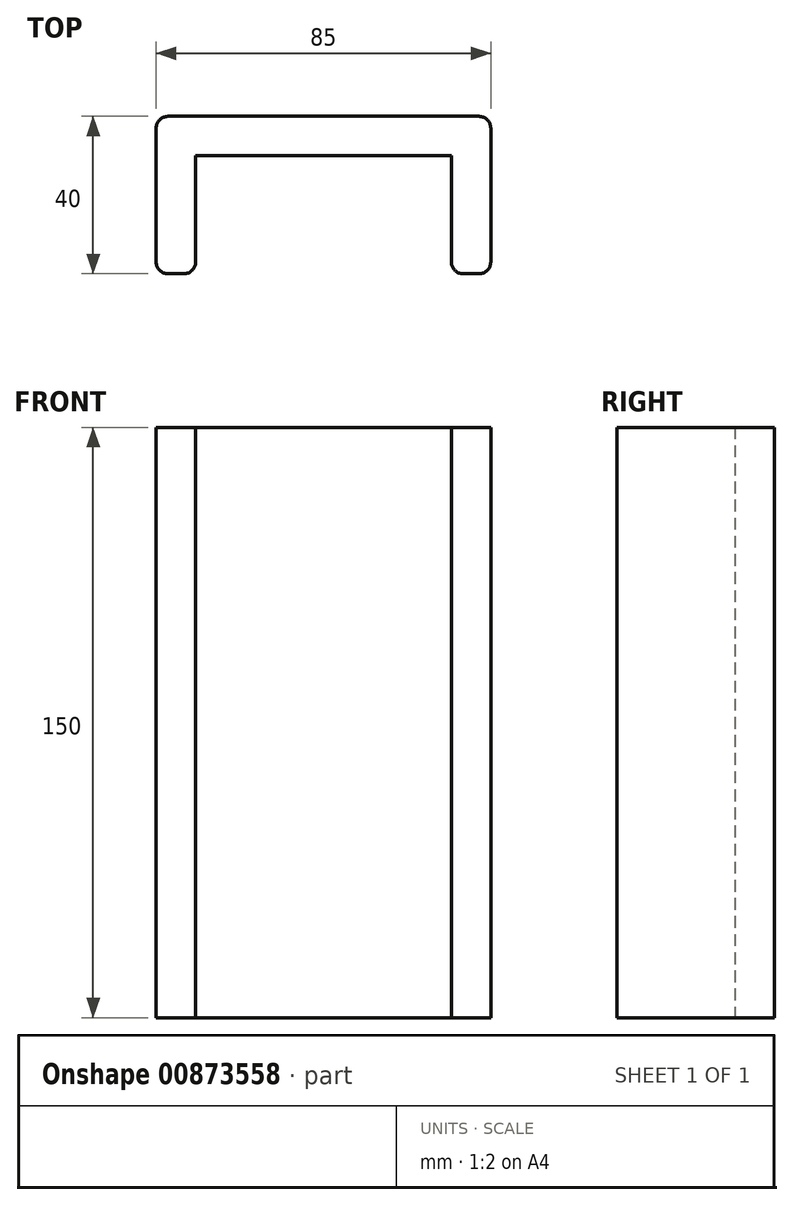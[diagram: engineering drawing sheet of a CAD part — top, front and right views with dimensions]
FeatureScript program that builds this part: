
annotation { "Feature Type Name" : "Feature", "Feature Type Description" : "" }
export const myFeature = defineFeature(function(context is Context, id is Id, definition is map)
    precondition{}
    {
        {
            var Q0;
            Q0=qCreatedBy(makeId("Top.planeOp"),FACE);
            var sketch = newSketch(context, id + "F0", { "sketchPlane" : qUnion([Q0])});
            skLineSegment(sketch, "E0.top", {"start": v(0, 30) * mm, "end": v(65, 30) * mm});
            skLineSegment(sketch, "E0.left", {"start": v(0, 0) * mm, "end": v(0, 30) * mm});
            skLineSegment(sketch, "E0.right", {"start": v(65, 0) * mm, "end": v(65, 30) * mm});
            skLineSegment(sketch, "E1.0", {"start": v(75, 0) * mm, "end": v(75, 40) * mm});
            skLineSegment(sketch, "E1.1", {"start": v(-10, 40) * mm, "end": v(75, 40) * mm});
            skLineSegment(sketch, "E1.2", {"start": v(-10, 0) * mm, "end": v(-10, 40) * mm});
            skLineSegment(sketch, "E2", {"start": v(75, 0) * mm, "end": v(65, 0) * mm});
            skLineSegment(sketch, "E3", {"start": v(0, 0) * mm, "end": v(-10, 0) * mm});
            skSolve(sketch);
        }
        {
            var Q0;
            Q0=makeQuery(id+"F0.imprint","IMPRINT",FACE,{"disambiguationData":[TD([[makeQuery(id+"F0.imprint","IMPRINT",EDGE,{"derivedFrom":sQuery(id+"F0.wireOp",EDGE,"E0.top")}),1.0]])]});
            extrude(context, id + "F1", {"entities" : qUnion([Q0]), "depth" : 150 * mm, "offsetDistance" : 25 * mm});
        }
        {
            var Q0;
            Q0=makeQuery(id+"F1.opExtrude","SWEPT_EDGE",EDGE,{"disambiguationData":[OSD([sQuery(id+"F0.wireOp",EDGE,"E1.1"),sQuery(id+"F0.wireOp",EDGE,"E1.2")])]});
            var Q1;
            Q1=makeQuery(id+"F1.opExtrude","SWEPT_EDGE",EDGE,{"disambiguationData":[OSD([sQuery(id+"F0.wireOp",EDGE,"E1.0"),sQuery(id+"F0.wireOp",EDGE,"E1.1")])]});
            var Q2;
            Q2=makeQuery(id+"F1.opExtrude","SWEPT_EDGE",EDGE,{"disambiguationData":[OSD([sQuery(id+"F0.wireOp",EDGE,"E1.2"),sQuery(id+"F0.wireOp",EDGE,"E3")])]});
            var Q3;
            Q3=makeQuery(id+"F1.opExtrude","SWEPT_EDGE",EDGE,{"disambiguationData":[OSD([sQuery(id+"F0.wireOp",EDGE,"E1.0"),sQuery(id+"F0.wireOp",EDGE,"E2")])]});
            var Q4;
            Q4=makeQuery(id+"F1.opExtrude","SWEPT_EDGE",EDGE,{"disambiguationData":[OSD([sQuery(id+"F0.wireOp",EDGE,"E0.right"),sQuery(id+"F0.wireOp",EDGE,"E2")])]});
            var Q5;
            Q5=makeQuery(id+"F1.opExtrude","SWEPT_EDGE",EDGE,{"disambiguationData":[OSD([sQuery(id+"F0.wireOp",EDGE,"E0.left"),sQuery(id+"F0.wireOp",EDGE,"E3")])]});
            fillet(context, id + "F2", {"entities" : qUnion([Q0, Q1, Q2, Q3, Q4, Q5]), "tangentPropagation" : true, "radius" : 3 * mm, "defaultsChanged" : false, "vertexSettings" : [], "allowEdgeOverflow" : false});
        }
    });
